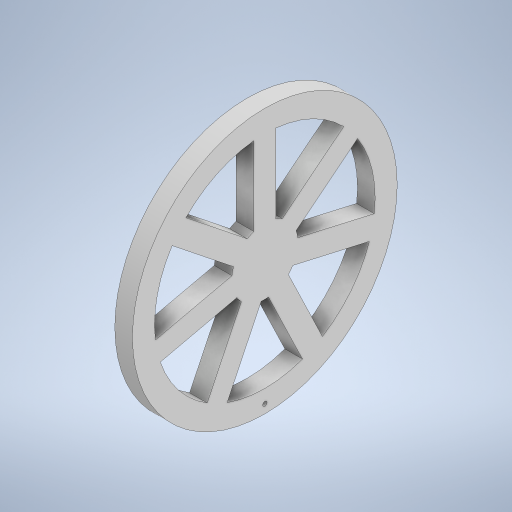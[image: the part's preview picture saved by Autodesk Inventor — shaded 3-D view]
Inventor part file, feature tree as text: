
AUTODESK INVENTOR PART (.ipt)
format: ipt  version: 2023.2 (Build 272271000, 271)  size: 334,848 bytes
history: native  units: mm
features: sketch x3
ambient origin geometry x8: Origin, YZ Plane, XZ Plane, XY Plane, X Axis, Y Axis, Z Axis, Center Point
bodies: Body1 (feature_tree)
feature tree (3):
  sketch  "Sketch1"  dims[d228=60.0mm]
  sketch  "Sketch2"  dims[d229=4.0mm d230=0.0mm]
  sketch  "Sketch3"  dims[d231=1.0mm d233=28.0mm d234=1.0mm d235=6.0mm d236=4.0mm d237=2.0mm d238=90.0deg d239=8.0mm d240=20.594885mm d251=15.0mm d252=5.0mm d257=4.0mm d258=0.0mm d259=5.0mm d260=70.0mm d262=360.0deg d9=0.5mm d10=0.872665mm d11=0.5mm d12=0.872665mm d13=0.5mm d14=0.872665mm d27=0.5mm d28=0.872665mm d29=0.5mm d30=0.872665mm d88=0.5mm d89=0.872665mm d90=0.5mm d91=0.872665mm d116=0.5mm d117=0.872665mm d118=0.5mm d119=0.872665mm d154=0.5mm d155=0.872665mm d156=0.5mm d157=0.872665mm d181=0.5mm d182=0.872665mm d183=0.5mm d184=0.872665mm d221=0.5mm d222=0.872665mm d223=0.5mm d224=0.872665mm]
